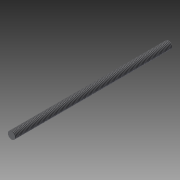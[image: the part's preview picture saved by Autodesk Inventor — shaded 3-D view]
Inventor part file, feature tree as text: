
AUTODESK INVENTOR PART (.ipt)
format: ipt  version: 2015 (Build 190159000, 159)  size: 73,728 bytes
history: native  units: in
note: dims shown in document units (in); Inventor stores cm internally (conversion verified against a paired STEP export)
features: plane x1, extrude x1, thread x1, sketch x1
ambient origin geometry x8: Origin, YZ Plane, XZ Plane, XY Plane, X Axis, Y Axis, Z Axis, Center Point
bodies: Solid1 (feature_tree)
feature tree (4):
  plane  "Work Plane1"
  extrude  "Extrusion1"  Depth=0.3937in TaperAngle=0.0deg
  thread  "Thread1"  [1 undecoded]
  sketch  "Sketch1"  dims[d0=0.1181in d1=2.3622in d2=0.1969in d3=0.0in d4=0.0in d5=0.3937in d6=0.0in]
note: 1 required parameter value undecoded (feature->parameter linkage not recoverable at this tier; creation-order binding heuristic only, values carry confidence <= 0.55)
